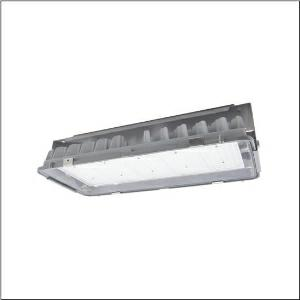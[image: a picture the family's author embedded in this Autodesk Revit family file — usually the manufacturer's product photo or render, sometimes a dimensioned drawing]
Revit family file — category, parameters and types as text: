
# Revit family: highbay_11xtreme_51hf62da4hma
name_source: partatom
category: Lighting Fixtures
units: mm (PartAtom-declared; Revit-internal decimal feet)

## family parameters
Cut with Voids When Loaded = No
Host = Face
Light Source = No
Part Type = Normal
Room Calculation Point = No
Round Connector Dimension = Use Diameter
Shared = No

## types (1)
- --- (1 x LED, 18500 lm, 96.5 W, 4000K)
    Apparent Load = 97 VA
    CIE Flux Codes = 84 96 100 100 100
    Color Rendering = 80
    Color Temperature = 4000K
    Default Elevation = 1800 mm
    Description = Highbay 11Xtreme, high bay luminaire, primary light control with lens, of PMMA, primary optical cover: cover, of toughened safety glass, light emission: direct distribution, primary light characteristic: symmetric, installation type: suspended mounting, surface-mounted, 1x LED module,for 1x LED, rated luminous flux: 18.500lm, luminous efficacy: 192lm/W, light colour: 840, colour temperature: 4000K, control gear: DALI 2, with cable H07RN-F 5x 1.5mm², mains connection: 220..240V, AC, 50/60Hz, cable length: 1,5m, rated input power: 97W, luminaire housing, of diecast aluminium, coated, silver, length: 595mm, width: 280mm, height: 195mm, protection rating (complete): IP66, insulation class (complete): insulation class I (protective earthing), certification: CE, ENEC, UKCA, protection symbol: D, ball protection: ball impact resistant according to DIN VDE 0710 part 13 (with chain suspension), impact resistance: IK08, permissible operating ambient temperature: -25..+70°C, reducing of maximum allowable ambient temperature of 5°C with ceiling mounting, packaging unit: 1 piece
    Height = 157 mm
    Lamp = 1 x LED
    Lamp Light Flux = 18500 lm
    Lamp Power = 96.5 W
    Lamp count = 1
    Length = 593 mm
    Luminous efficacy = 192 lm/W
    Manufacturer = Siteco
    ModVariant = No
    Model = 51HF62DA4HMA
    Mounting Place = Ceiling
    Mounting Type = Pendant
    Number of Poles = 1
    OnlyDefault = Yes
    Power Factor = 1
    Product Name = Highbay 11Xtreme
    Product group = high bay luminaire
    ProductGroupID = 902
    Protection Class = Protection class I
    Protection Degree = IP 66
    RLX_Detail_Level = 1
    RLX_Emergency_Light_Flux = 0 lm
    RLX_Emergency_Type = 0
    RLX_Emergency_Type_DB = No
    RlxData = <blob elided: 28293 chars, md5=90000e6a>
    Socket = socket
    Standby Power = 0 W
    System Light Flux = 18500 lm
    System Power = 97 W
    Type Comments = factory setting: luminous flux: 100 % | dim-lin: 254 | 652 mA
    Type Image = l_1258342.jpg
    URL = http://relux.com
    VarID = @adj_088365
    Voltage = 0 V
    Weight = 0.00 kg
    Width = 568 mm

## geometry (parser evidence)
native form markers: Blend x4, Sweep x10
no freeform markers — native parametric forms only
